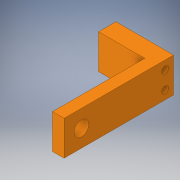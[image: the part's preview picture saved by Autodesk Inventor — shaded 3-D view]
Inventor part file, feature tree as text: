
AUTODESK INVENTOR PART (.ipt)
format: ipt  version: 2019 (Build 230136000, 136)  size: 122,368 bytes
history: native  units: in
note: dims shown in document units (in); Inventor stores cm internally (conversion verified against a paired STEP export)
features: sketch x3, hole x2, projected_geometry x2, extrude x1
ambient origin geometry x8: Origin, YZ Plane, XZ Plane, XY Plane, X Axis, Y Axis, Z Axis, Center Point
bodies: Solid1 (feature_tree)
feature tree (8):
  extrude  "Extrusion1"  Depth=1.25in
  hole  "Hole1"  [1 undecoded]
  hole  "Hole2"  [1 undecoded]
  sketch  "Sketch1"  dims[d0=2.375in d1=1.25in]
  sketch  "Sketch2"  dims[d2=0.375in d3=0.25in]
  projected_geometry  "Projected Loop1"
  sketch  "Sketch3"  dims[d4=0.75in d5=0.0in d6=0.75in d7=0.375in d8=0.375in d9=0.32in d10=0.75in d11=0.375in d12=0.25in d13=0.5635in d14=0.432in d15=0.8108in d16=0.375in d17=0.375in d18=0.1875in d19=0.75in d20=0.1875in d21=0.1875in d22=0.15in d23=0.75in d24=0.375in d25=0.25in d26=0.5635in d27=0.432in d28=0.8108in]
  projected_geometry  "Projected Loop2"
note: 2 required parameter values undecoded (feature->parameter linkage not recoverable at this tier; creation-order binding heuristic only, values carry confidence <= 0.55)
